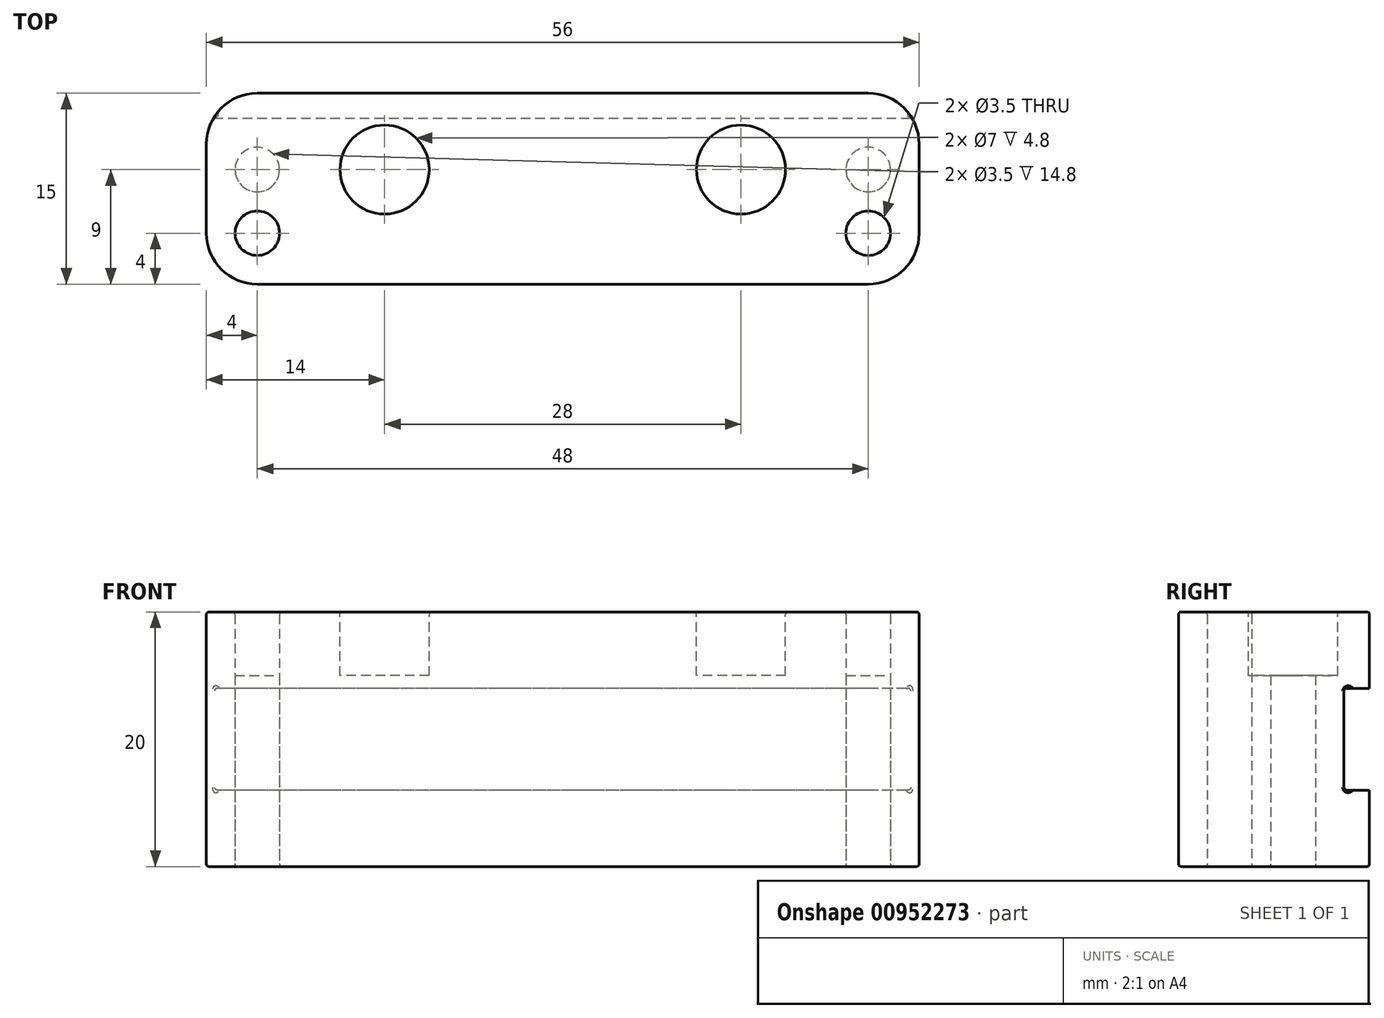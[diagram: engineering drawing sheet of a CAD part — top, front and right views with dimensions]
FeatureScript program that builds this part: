
annotation { "Feature Type Name" : "Feature", "Feature Type Description" : "" }
export const myFeature = defineFeature(function(context is Context, id is Id, definition is map)
    precondition{}
    {
        {
            var Q0;
            Q0=qCreatedBy(makeId("Top.planeOp"),FACE);
            var sketch = newSketch(context, id + "F0", { "sketchPlane" : qUnion([Q0])});
            skPoint(sketch, "E0.middle", {"position": v(0, 0) * mm});
            skCircle(sketch, "E1", {"center": v(-24, 4) * mm, "radius": 1.75 * mm});
            skCircle(sketch, "E2.MirrorC", {"center": v(24, 4) * mm, "radius": 1.75 * mm});
            skLineSegment(sketch, "E3", {"start": v(-28, 15) * mm, "end": v(-28, 0) * mm});
            skLineSegment(sketch, "E4.MirrorCS", {"start": v(28, 15) * mm, "end": v(28, 0) * mm});
            skLineSegment(sketch, "E5", {"start": v(-28, 15) * mm, "end": v(28, 15) * mm});
            skLineSegment(sketch, "E6.bottom", {"start": v(28, 15) * mm, "end": v(-28, 15) * mm});
            skLineSegment(sketch, "E6.top", {"start": v(28, 23) * mm, "end": v(-28, 23) * mm});
            skLineSegment(sketch, "E6.left", {"start": v(28, 15) * mm, "end": v(28, 23) * mm});
            skLineSegment(sketch, "E6.right", {"start": v(-28, 15) * mm, "end": v(-28, 23) * mm});
            skLineSegment(sketch, "E7", {"start": v(-10.46, 11.5) * mm, "end": v(-13.31, 11.5) * mm});
            skCircle(sketch, "E8.MirrorC", {"center": v(-24, 19) * mm, "radius": 1.75 * mm});
            skCircle(sketch, "E9.MirrorC", {"center": v(24, 19) * mm, "radius": 1.75 * mm});
            skLineSegment(sketch, "E10", {"start": v(-28, 0) * mm, "end": v(28, 0) * mm});
            skSolve(sketch);
        }
        {
            var Q0;
            {var subQ5=sQuery(id+"F0.wireOp",EDGE,"11D1waYO-lteK-NlZX-o6ij-neL2n2zAW9KT.bottom");var subQ9=sQuery(id+"F0.wireOp",EDGE,"E1");var subQ10=makeQuery(id+"F0.imprint","INTERSECT",VERTEX,{"derivedFrom":[subQ9,subQ5]});Q0=makeQuery(id+"F0.imprint","IMPRINT",FACE,{"disambiguationData":[TD([[makeQuery(id+"F0.imprint","IMPRINT",EDGE,{"disambiguationData":[TD([[subQ10,1.0]])],"derivedFrom":subQ9}),-1.0]])]});}
            var Q1;
            {var subQ0=sQuery(id+"F0.wireOp",EDGE,"E3");Q1=makeQuery(id+"F0.imprint","IMPRINT",FACE,{"disambiguationData":[TD([[makeQuery(id+"F0.imprint","IMPRINT",EDGE,{"derivedFrom":subQ0}),1.0]])]});}
            var Q2;
            Q2=makeQuery(id+"F0.imprint","IMPRINT",FACE,{"disambiguationData":[TD([[makeQuery(id+"F0.imprint","IMPRINT",EDGE,{"derivedFrom":sQuery(id+"F0.wireOp",EDGE,"E6.bottom")}),-1.0]])]});
            var Q3;
            {var subQ0=sQuery(id+"F0.wireOp",EDGE,"E3");Q3=makeQuery(id+"F0.imprint","IMPRINT",FACE,{"disambiguationData":[TD([[makeQuery(id+"F0.imprint","IMPRINT",EDGE,{"derivedFrom":subQ0}),1.0]])]});}
            extrude(context, id + "F1", {"entities" : qUnion([Q0, Q1, Q2, Q3]), "depth" : 20 * mm, "offsetDistance" : 25 * mm, "symmetric" : true});
        }
        {
            var Q0;
            Q0=makeQuery(id+"F1.opExtrude","CAP_FACE",FACE,{"disambiguationData":[OSD([sQuery(id+"F0.wireOp",EDGE,"E0.top"),sQuery(id+"F0.wireOp",EDGE,"E1"),sQuery(id+"F0.wireOp",EDGE,"E2.MirrorC"),sQuery(id+"F0.wireOp",EDGE,"E3"),sQuery(id+"F0.wireOp",EDGE,"E4.MirrorCS"),sQuery(id+"F0.wireOp",EDGE,"c8v4qdNd-6dEN-1ngM-11SU-dZ9w3vu84ArM"),sQuery(id+"F0.wireOp",EDGE,"48b92598-7f4e-4252-9e84-3900e4211c050.MirrorC"),sQuery(id+"F0.wireOp",EDGE,"Hcgi889i-RzIl-pvt1-SlOf-mdv69IkWLDyQ.bottom"),sQuery(id+"F0.wireOp",EDGE,"Hcgi889i-RzIl-pvt1-SlOf-mdv69IkWLDyQ.top"),sQuery(id+"F0.wireOp",EDGE,"Hcgi889i-RzIl-pvt1-SlOf-mdv69IkWLDyQ.left"),sQuery(id+"F0.wireOp",EDGE,"Hcgi889i-RzIl-pvt1-SlOf-mdv69IkWLDyQ.right")])],"isStart":false});
            var sketch = newSketch(context, id + "F2", { "sketchPlane" : qUnion([Q0])});
            skCircle(sketch, "E11", {"center": v(-14, 9) * mm, "radius": 3.5 * mm});
            skCircle(sketch, "E12.MirrorC", {"center": v(14, 9) * mm, "radius": 3.5 * mm});
            skLineSegment(sketch, "E13", {"start": v(-24, 4) * mm, "end": v(-7.64, 4) * mm});
            skSolve(sketch);
        }
        {
            var Q0;
            Q0 = qSketchRegion(id + "F2", true);
            extrude(context, id + "F3", {"entities" : qUnion([Q0]), "operationType" : NewBodyOperationType.REMOVE, "oppositeDirection" : true, "depth" : 5 * mm, "offsetDistance" : 25 * mm});
        }
        {
            var Q0;
            Q0=makeQuery(id+"F1.opExtrude","SWEPT_FACE",FACE,{"disambiguationData":[OSD([sQuery(id+"F0.wireOp",EDGE,"E3"),sQuery(id+"F0.wireOp",EDGE,"E6.right")])]});
            var sketch = newSketch(context, id + "F4", { "sketchPlane" : qUnion([Q0])});
            skLineSegment(sketch, "E14.bottom", {"start": v(-13, 4) * mm, "end": v(-33, 4) * mm});
            skLineSegment(sketch, "E14.top", {"start": v(-13, -4) * mm, "end": v(-33, -4) * mm});
            skLineSegment(sketch, "E14.left", {"start": v(-13, 4) * mm, "end": v(-13, -4) * mm});
            skLineSegment(sketch, "E14.right", {"start": v(-33, 4) * mm, "end": v(-33, -4) * mm});
            skPoint(sketch, "E14.middle", {"position": v(-23, 0) * mm});
            skSolve(sketch);
        }
        {
            var Q0;
            Q0=makeQuery(id+"F1.opExtrude","SWEPT_EDGE",EDGE,{"disambiguationData":[OSD([sQuery(id+"F0.wireOp",EDGE,"Hcgi889i-RzIl-pvt1-SlOf-mdv69IkWLDyQ.bottom"),sQuery(id+"F0.wireOp",EDGE,"Hcgi889i-RzIl-pvt1-SlOf-mdv69IkWLDyQ.right")])]});
            var Q1;
            Q1=makeQuery(id+"F1.opExtrude","SWEPT_EDGE",EDGE,{"disambiguationData":[OSD([sQuery(id+"F0.wireOp",EDGE,"Hcgi889i-RzIl-pvt1-SlOf-mdv69IkWLDyQ.top"),sQuery(id+"F0.wireOp",EDGE,"Hcgi889i-RzIl-pvt1-SlOf-mdv69IkWLDyQ.right")])]});
            var Q2;
            Q2=makeQuery(id+"F1.opExtrude","SWEPT_EDGE",EDGE,{"disambiguationData":[OSD([sQuery(id+"F0.wireOp",EDGE,"Hcgi889i-RzIl-pvt1-SlOf-mdv69IkWLDyQ.top"),sQuery(id+"F0.wireOp",EDGE,"Hcgi889i-RzIl-pvt1-SlOf-mdv69IkWLDyQ.left")])]});
            var Q3;
            Q3=makeQuery(id+"F1.opExtrude","SWEPT_EDGE",EDGE,{"disambiguationData":[OSD([sQuery(id+"F0.wireOp",EDGE,"Hcgi889i-RzIl-pvt1-SlOf-mdv69IkWLDyQ.bottom"),sQuery(id+"F0.wireOp",EDGE,"Hcgi889i-RzIl-pvt1-SlOf-mdv69IkWLDyQ.left")])]});
            var Q4;
            Q4=makeQuery(id+"F1.opExtrude","SWEPT_EDGE",EDGE,{"disambiguationData":[OSD([sQuery(id+"F0.wireOp",EDGE,"E6.top"),sQuery(id+"F0.wireOp",EDGE,"E6.right")])]});
            var Q5;
            Q5=makeQuery(id+"F1.opExtrude","SWEPT_EDGE",EDGE,{"disambiguationData":[OSD([sQuery(id+"F0.wireOp",EDGE,"E6.top"),sQuery(id+"F0.wireOp",EDGE,"E6.left")])]});
            var Q6;
            Q6=makeQuery(id+"F1.opExtrude","SWEPT_EDGE",EDGE,{"disambiguationData":[OSD([sQuery(id+"F0.wireOp",EDGE,"E3"),sQuery(id+"F0.wireOp",EDGE,"E10")])]});
            var Q7;
            Q7=makeQuery(id+"F1.opExtrude","SWEPT_EDGE",EDGE,{"disambiguationData":[OSD([sQuery(id+"F0.wireOp",EDGE,"E4.MirrorCS"),sQuery(id+"F0.wireOp",EDGE,"E10")])]});
            fillet(context, id + "F5", {"entities" : qUnion([Q0, Q1, Q2, Q3, Q4, Q5, Q6, Q7]), "tangentPropagation" : true, "radius" : 4 * mm, "defaultsChanged" : false, "vertexSettings" : [], "allowEdgeOverflow" : false});
        }
        {
            var Q0;
            {var subQ0=sQuery(id+"F4.wireOp",EDGE,"E14.left");Q0=makeQuery(id+"F4.imprint","IMPRINT",FACE,{"disambiguationData":[TD([[makeQuery(id+"F4.imprint","IMPRINT",EDGE,{"derivedFrom":subQ0}),-1.0]])]});}
            extrude(context, id + "F6", {"entities" : qUnion([Q0]), "operationType" : NewBodyOperationType.REMOVE, "endBound" : BoundingType.THROUGH_ALL, "oppositeDirection" : true, "depth" : 25 * mm, "offsetDistance" : 25 * mm});
        }
        {
            var Q0;
            Q0=makeQuery(id+"F1.opExtrude","CAP_FACE",FACE,{"disambiguationData":[OSD([sQuery(id+"F0.wireOp",EDGE,"E1"),sQuery(id+"F0.wireOp",EDGE,"E2.MirrorC"),sQuery(id+"F0.wireOp",EDGE,"E3"),sQuery(id+"F0.wireOp",EDGE,"E4.MirrorCS"),sQuery(id+"F0.wireOp",EDGE,"E6.top"),sQuery(id+"F0.wireOp",EDGE,"E6.left"),sQuery(id+"F0.wireOp",EDGE,"E6.right"),sQuery(id+"F0.wireOp",EDGE,"E8.MirrorC"),sQuery(id+"F0.wireOp",EDGE,"E9.MirrorC"),sQuery(id+"F0.wireOp",EDGE,"E10")])],"isStart":true});
            var sketch = newSketch(context, id + "F7", { "sketchPlane" : qUnion([Q0])});
            skCircle(sketch, "E15", {"center": v(24, -9) * mm, "radius": 1.75 * mm});
            skLineSegment(sketch, "E16", {"start": v(24, -9) * mm, "end": v(24, -4) * mm});
            skCircle(sketch, "E17.MirrorC", {"center": v(-24, -9) * mm, "radius": 1.75 * mm});
            skSolve(sketch);
        }
        {
            var Q0;
            Q0 = qSketchRegion(id + "F7", true);
            extrude(context, id + "F8", {"entities" : qUnion([Q0]), "operationType" : NewBodyOperationType.REMOVE, "oppositeDirection" : true, "depth" : 15 * mm, "offsetDistance" : 25 * mm});
        }
        {
            var Q0;
            Q0=makeQuery(id+"F1.opExtrude","CAP_FACE",FACE,{"disambiguationData":[OSD([sQuery(id+"F0.wireOp",EDGE,"E1"),sQuery(id+"F0.wireOp",EDGE,"E2.MirrorC"),sQuery(id+"F0.wireOp",EDGE,"E3"),sQuery(id+"F0.wireOp",EDGE,"E4.MirrorCS"),sQuery(id+"F0.wireOp",EDGE,"E6.top"),sQuery(id+"F0.wireOp",EDGE,"E6.left"),sQuery(id+"F0.wireOp",EDGE,"E6.right"),sQuery(id+"F0.wireOp",EDGE,"E8.MirrorC"),sQuery(id+"F0.wireOp",EDGE,"E9.MirrorC"),sQuery(id+"F0.wireOp",EDGE,"E10")])],"isStart":false});
            var Q1;
            Q1=makeQuery(id+"F1.opExtrude","SWEPT_FACE",FACE,{"disambiguationData":[OSD([sQuery(id+"F0.wireOp",EDGE,"E3"),sQuery(id+"F0.wireOp",EDGE,"E6.right")])]});
            var Q2;
            Q2=makeQuery(id+"F1.opExtrude","CAP_FACE",FACE,{"disambiguationData":[OSD([sQuery(id+"F0.wireOp",EDGE,"E1"),sQuery(id+"F0.wireOp",EDGE,"E2.MirrorC"),sQuery(id+"F0.wireOp",EDGE,"E3"),sQuery(id+"F0.wireOp",EDGE,"E4.MirrorCS"),sQuery(id+"F0.wireOp",EDGE,"E6.top"),sQuery(id+"F0.wireOp",EDGE,"E6.left"),sQuery(id+"F0.wireOp",EDGE,"E6.right"),sQuery(id+"F0.wireOp",EDGE,"E8.MirrorC"),sQuery(id+"F0.wireOp",EDGE,"E9.MirrorC"),sQuery(id+"F0.wireOp",EDGE,"E10")])],"isStart":true});
            var Q3;
            Q3=makeQuery(id+"F6.boolean.opBoolean","COPY",FACE,{"derivedFrom":makeQuery(id+"F6.opExtrude","SWEPT_FACE",FACE,{"disambiguationData":[OSD([sQuery(id+"F4.wireOp",EDGE,"E14.left")])]})});
            fillet(context, id + "F9", {"entities" : qUnion([Q0, Q1, Q2, Q3]), "tangentPropagation" : true, "radius" : 0.2 * mm, "defaultsChanged" : false, "vertexSettings" : [], "allowEdgeOverflow" : false});
        }
    });
